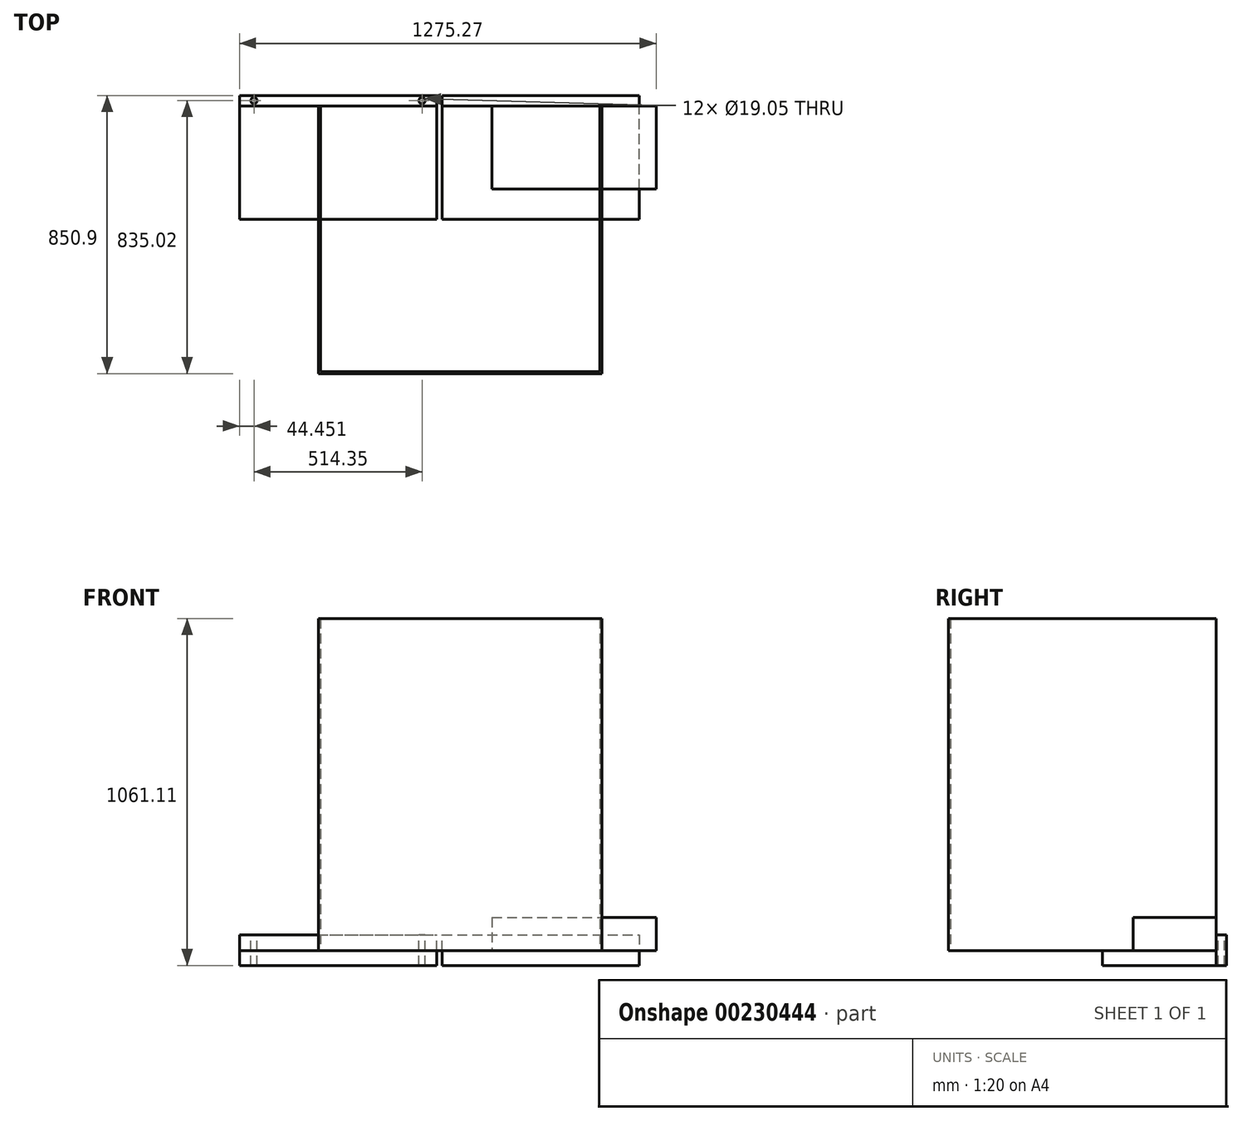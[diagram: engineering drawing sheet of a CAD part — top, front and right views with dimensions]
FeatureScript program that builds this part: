
annotation { "Feature Type Name" : "Feature", "Feature Type Description" : "" }
export const myFeature = defineFeature(function(context is Context, id is Id, definition is map)
    precondition{}
    {
        {
            var Q0;
            Q0=qCreatedBy(makeId("Top.planeOp"),FACE);
            var sketch = newSketch(context, id + "F0", { "sketchPlane" : qUnion([Q0])});
            skLineSegment(sketch, "E0.bottom", {"start": v(-614.1, -340.38) * mm, "end": v(609.86, -340.38) * mm});
            skLineSegment(sketch, "E0.top", {"start": v(-614.1, 7.29) * mm, "end": v(609.86, 7.29) * mm});
            skLineSegment(sketch, "E0.left", {"start": v(-614.1, -340.38) * mm, "end": v(-614.1, 7.29) * mm});
            skLineSegment(sketch, "E0.right", {"start": v(609.86, -340.38) * mm, "end": v(609.86, 7.29) * mm});
            skSolve(sketch);
        }
        {
            var Q0;
            Q0 = qSketchRegion(id + "F0", true);
            extrude(context, id + "F1", {"entities" : qUnion([Q0]), "oppositeDirection" : true, "depth" : 45.1 * mm});
        }
        {
            var Q0;
            Q0=makeQuery(id+"F1.opExtrude","CAP_FACE",FACE,{"disambiguationData":[OSD([sQuery(id+"F0.wireOp",EDGE,"E0.bottom"),sQuery(id+"F0.wireOp",EDGE,"E0.top"),sQuery(id+"F0.wireOp",EDGE,"E0.left"),sQuery(id+"F0.wireOp",EDGE,"E0.right")])],"isStart":true});
            cPlane(context, id + "F2", {"entities" : qUnion([Q0]), "cplaneType" : CPlaneType.OFFSET, "offset" : 45.1 * mm, "oppositeDirection" : true, "width" : 152.4 * mm, "height" : 152.4 * mm});
        }
        {
            var Q0;
            Q0=qCreatedBy(id+"F2.planeOp",FACE);
            var sketch = newSketch(context, id + "F3", { "sketchPlane" : qUnion([Q0])});
            skLineSegment(sketch, "E1.bottom", {"start": v(-614.1, 7.29) * mm, "end": v(609.86, 7.29) * mm});
            skLineSegment(sketch, "E1.top", {"start": v(-614.1, 39.04) * mm, "end": v(609.86, 39.04) * mm});
            skLineSegment(sketch, "E1.left", {"start": v(-614.1, 7.29) * mm, "end": v(-614.1, 39.04) * mm});
            skLineSegment(sketch, "E1.right", {"start": v(609.86, 7.29) * mm, "end": v(609.86, 39.04) * mm});
            skSolve(sketch);
        }
        {
            var Q0;
            Q0 = qSketchRegion(id + "F3", true);
            extrude(context, id + "F4", {"entities" : qUnion([Q0]), "depth" : 94 * mm});
        }
        {
            var Q0;
            Q0=makeQuery(id+"F4.opExtrude","CAP_FACE",FACE,{"disambiguationData":[OSD([sQuery(id+"F3.wireOp",EDGE,"E1.bottom"),sQuery(id+"F3.wireOp",EDGE,"E1.top"),sQuery(id+"F3.wireOp",EDGE,"E1.left"),sQuery(id+"F3.wireOp",EDGE,"E1.right")])],"isStart":false});
            var sketch = newSketch(context, id + "F5", { "sketchPlane" : qUnion([Q0])});
            skLineSegment(sketch, "E2.bottom", {"start": v(-10.85, 39.04) * mm, "end": v(6.68, 39.04) * mm});
            skLineSegment(sketch, "E2.top", {"start": v(-10.85, -340.38) * mm, "end": v(6.68, -340.38) * mm});
            skLineSegment(sketch, "E2.left", {"start": v(-10.85, 39.04) * mm, "end": v(-10.85, -340.38) * mm});
            skLineSegment(sketch, "E2.right", {"start": v(6.68, 39.04) * mm, "end": v(6.68, -340.38) * mm});
            skSolve(sketch);
        }
        {
            var Q0;
            Q0 = qSketchRegion(id + "F5", true);
            extrude(context, id + "F6", {"entities" : qUnion([Q0]), "operationType" : NewBodyOperationType.REMOVE, "endBound" : BoundingType.THROUGH_ALL, "oppositeDirection" : true, "depth" : 25.4 * mm});
        }
        {
            var Q0;
            {var subQ0=sQuery(id+"F0.wireOp",EDGE,"E0.bottom");var subQ1=sQuery(id+"F0.wireOp",EDGE,"E0.top");var subQ2=sQuery(id+"F0.wireOp",EDGE,"E0.left");Q0=makeQuery(id+"F6.boolean.opBoolean","SPLIT",FACE,{"disambiguationData":[TD([makeQuery(id+"F1.opExtrude","SWEPT_FACE",FACE,{"disambiguationData":[OSD([subQ2])]})])],"derivedFrom":makeQuery(id+"F1.opExtrude","CAP_FACE",FACE,{"disambiguationData":[OSD([subQ0,subQ1,subQ2,sQuery(id+"F0.wireOp",EDGE,"E0.right")])],"isStart":true})});}
            var sketch = newSketch(context, id + "F7", { "sketchPlane" : qUnion([Q0])});
            skLineSegment(sketch, "E3.bottom", {"start": v(-372.8, 7.29) * mm, "end": v(-366.45, 7.29) * mm});
            skLineSegment(sketch, "E3.top", {"start": v(-372.8, -811.86) * mm, "end": v(-366.45, -811.86) * mm});
            skLineSegment(sketch, "E3.left", {"start": v(-372.8, 7.29) * mm, "end": v(-372.8, -811.86) * mm});
            skLineSegment(sketch, "E3.right", {"start": v(-366.45, 7.29) * mm, "end": v(-366.45, -811.86) * mm});
            skLineSegment(sketch, "E4.bottom", {"start": v(495.56, 7.29) * mm, "end": v(489.21, 7.29) * mm});
            skLineSegment(sketch, "E4.top", {"start": v(495.56, -811.86) * mm, "end": v(489.21, -811.86) * mm});
            skLineSegment(sketch, "E4.left", {"start": v(495.56, 7.29) * mm, "end": v(495.56, -811.86) * mm});
            skLineSegment(sketch, "E4.right", {"start": v(489.21, 7.29) * mm, "end": v(489.21, -811.86) * mm});
            skLineSegment(sketch, "E5.bottom", {"start": v(-372.8, -811.86) * mm, "end": v(495.56, -811.86) * mm});
            skLineSegment(sketch, "E5.top", {"start": v(-372.8, -805.51) * mm, "end": v(495.56, -805.51) * mm});
            skLineSegment(sketch, "E5.left", {"start": v(-372.8, -811.86) * mm, "end": v(-372.8, -805.51) * mm});
            skLineSegment(sketch, "E5.right", {"start": v(495.56, -811.86) * mm, "end": v(495.56, -805.51) * mm});
            skSolve(sketch);
        }
        {
            var Q0;
            Q0 = qSketchRegion(id + "F7", true);
            extrude(context, id + "F8", {"entities" : qUnion([Q0]), "depth" : 1016 * mm});
        }
        {
            var Q0;
            {var subQ0=sQuery(id+"F0.wireOp",EDGE,"E0.bottom");var subQ1=sQuery(id+"F0.wireOp",EDGE,"E0.top");var subQ2=sQuery(id+"F0.wireOp",EDGE,"E0.right");Q0=makeQuery(id+"F6.boolean.opBoolean","SPLIT",FACE,{"disambiguationData":[TD([makeQuery(id+"F1.opExtrude","SWEPT_FACE",FACE,{"disambiguationData":[OSD([subQ2])]})])],"derivedFrom":makeQuery(id+"F1.opExtrude","CAP_FACE",FACE,{"disambiguationData":[OSD([subQ0,subQ1,sQuery(id+"F0.wireOp",EDGE,"E0.left"),subQ2])],"isStart":true})});}
            var sketch = newSketch(context, id + "F9", { "sketchPlane" : qUnion([Q0])});
            skLineSegment(sketch, "E6.bottom", {"start": v(159.08, 7.29) * mm, "end": v(661.17, 7.29) * mm});
            skLineSegment(sketch, "E6.top", {"start": v(159.08, -246.71) * mm, "end": v(661.17, -246.71) * mm});
            skLineSegment(sketch, "E6.left", {"start": v(159.08, 7.29) * mm, "end": v(159.08, -246.71) * mm});
            skLineSegment(sketch, "E6.right", {"start": v(661.17, 7.29) * mm, "end": v(661.17, -246.71) * mm});
            skSolve(sketch);
        }
        {
            var Q0;
            Q0 = qSketchRegion(id + "F9", true);
            extrude(context, id + "F10", {"entities" : qUnion([Q0]), "depth" : 101.6 * mm});
        }
        {
            var Q0;
            {var subQ0=sQuery(id+"F3.wireOp",EDGE,"E1.bottom");var subQ1=sQuery(id+"F3.wireOp",EDGE,"E1.top");var subQ2=sQuery(id+"F3.wireOp",EDGE,"E1.left");Q0=makeQuery(id+"F6.boolean.opBoolean","SPLIT",FACE,{"disambiguationData":[TD([makeQuery(id+"F4.opExtrude","SWEPT_FACE",FACE,{"disambiguationData":[OSD([subQ2])]})])],"derivedFrom":makeQuery(id+"F4.opExtrude","CAP_FACE",FACE,{"disambiguationData":[OSD([subQ0,subQ1,subQ2,sQuery(id+"F3.wireOp",EDGE,"E1.right")])],"isStart":false})});}
            var sketch = newSketch(context, id + "F11", { "sketchPlane" : qUnion([Q0])});
            skCircle(sketch, "E7", {"center": v(-569.65, 23.16) * mm, "radius": 9.53 * mm});
            skPoint(sketch, "E7.centerSnap0", {"position": v(-614.1, 23.16) * mm});
            skCircle(sketch, "E8", {"center": v(-55.3, 23.16) * mm, "radius": 9.53 * mm});
            skPoint(sketch, "E8.centerSnap0", {"position": v(-10.85, 23.16) * mm});
            skSolve(sketch);
        }
        {
            var Q0;
            Q0 = qSketchRegion(id + "F11", true);
            extrude(context, id + "F12", {"entities" : qUnion([Q0]), "operationType" : NewBodyOperationType.REMOVE, "endBound" : BoundingType.THROUGH_ALL, "oppositeDirection" : true, "depth" : 25.4 * mm});
        }
    });
